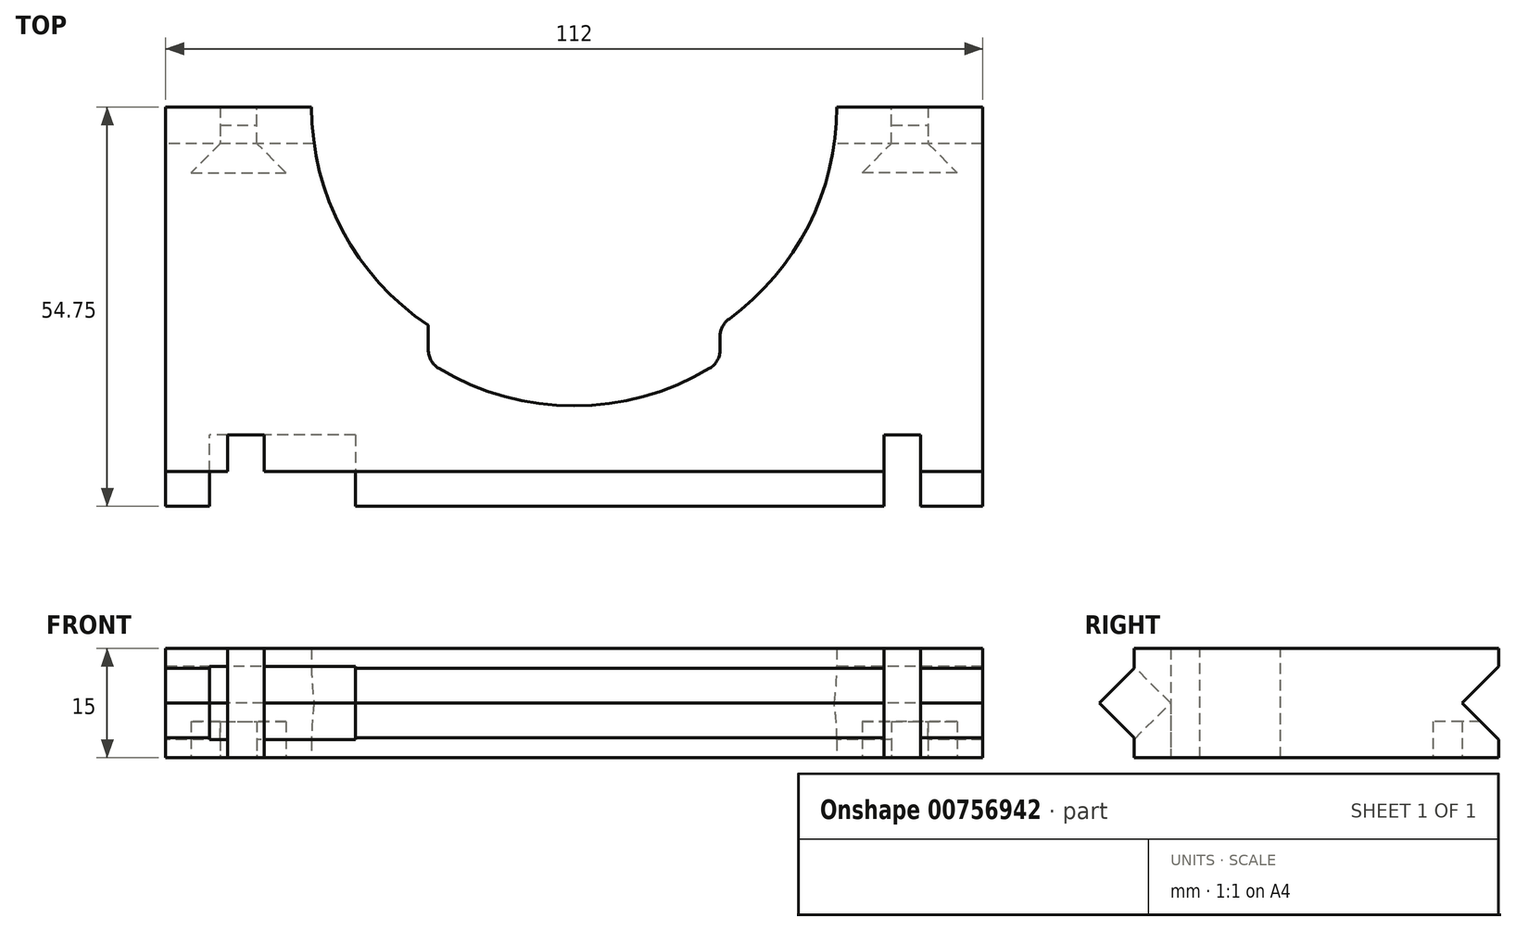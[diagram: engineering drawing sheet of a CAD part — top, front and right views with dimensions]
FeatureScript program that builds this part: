
annotation { "Feature Type Name" : "Feature", "Feature Type Description" : "" }
export const myFeature = defineFeature(function(context is Context, id is Id, definition is map)
    precondition{}
    {
        {
            var Q0;
            Q0=qCreatedBy(makeId("Top.planeOp"),FACE);
            var sketch = newSketch(context, id + "F0", { "sketchPlane" : qUnion([Q0])});
            skLineSegment(sketch, "E0", {"start": v(-56, 0) * mm, "end": v(56, 0) * mm});
            skLineSegment(sketch, "E1", {"start": v(56, 0) * mm, "end": v(56, 50) * mm});
            skLineSegment(sketch, "E2", {"start": v(56, 50) * mm, "end": v(36, 50) * mm});
            skLineSegment(sketch, "E3", {"start": v(-56, 0) * mm, "end": v(-56, 50) * mm});
            skLineSegment(sketch, "E4", {"start": v(-56, 50) * mm, "end": v(-36, 50) * mm});
            skArc(sketch, "E5", {"start": v(-36, 50) * mm, "mid": v(0, 14) * mm, "end": v(36, 50) * mm});
            skSolve(sketch);
        }
        {
            var Q0;
            Q0 = qSketchRegion(id + "F0", true);
            extrude(context, id + "F1", {"entities" : qUnion([Q0]), "depth" : 15 * mm, "offsetDistance" : 25 * mm});
        }
        {
            var Q0;
            Q0=makeQuery(id+"F1.opExtrude","SWEPT_FACE",FACE,{"disambiguationData":[OSD([sQuery(id+"F0.wireOp",EDGE,"E3")])]});
            var sketch = newSketch(context, id + "F2", { "sketchPlane" : qUnion([Q0])});
            skLineSegment(sketch, "E6", {"start": v(-50, 2.5) * mm, "end": v(-45, 7.5) * mm});
            skPoint(sketch, "E6.endSnap0", {"position": v(-50, 7.5) * mm});
            skLineSegment(sketch, "E7", {"start": v(-45, 7.5) * mm, "end": v(-50, 12.5) * mm});
            skLineSegment(sketch, "E8", {"start": v(-50, 12.5) * mm, "end": v(-50, 2.5) * mm});
            skSolve(sketch);
        }
        {
            var Q0;
            Q0 = qSketchRegion(id + "F2", true);
            extrude(context, id + "F3", {"entities" : qUnion([Q0]), "operationType" : NewBodyOperationType.REMOVE, "endBound" : BoundingType.THROUGH_ALL, "oppositeDirection" : true, "depth" : 25 * mm, "offsetDistance" : 25 * mm});
        }
        {
            var Q0;
            Q0=makeQuery(id+"F1.opExtrude","CAP_FACE",FACE,{"disambiguationData":[OSD([sQuery(id+"F0.wireOp",EDGE,"E0"),sQuery(id+"F0.wireOp",EDGE,"E1"),sQuery(id+"F0.wireOp",EDGE,"E2"),sQuery(id+"F0.wireOp",EDGE,"E3"),sQuery(id+"F0.wireOp",EDGE,"E4"),sQuery(id+"F0.wireOp",EDGE,"E5")])],"isStart":true});
            var sketch = newSketch(context, id + "F4", { "sketchPlane" : qUnion([Q0])});
            skLineSegment(sketch, "E9", {"start": v(-48.5, -50) * mm, "end": v(-48.5, -45) * mm});
            skLineSegment(sketch, "E10", {"start": v(-48.5, -45) * mm, "end": v(-52.5, -41) * mm});
            skLineSegment(sketch, "E11", {"start": v(-52.5, -41) * mm, "end": v(-39.5, -41) * mm});
            skLineSegment(sketch, "E12", {"start": v(-39.5, -41) * mm, "end": v(-43.5, -45) * mm});
            skLineSegment(sketch, "E13", {"start": v(-43.5, -45) * mm, "end": v(-43.5, -50) * mm});
            skLineSegment(sketch, "E14", {"start": v(-43.5, -50) * mm, "end": v(-48.5, -50) * mm});
            skLineSegment(sketch, "E15.MirrorCS", {"start": v(52.5, -41) * mm, "end": v(39.5, -41) * mm});
            skLineSegment(sketch, "E16.MirrorCS", {"start": v(48.5, -45) * mm, "end": v(52.5, -41) * mm});
            skLineSegment(sketch, "E17.MirrorCS", {"start": v(39.5, -41) * mm, "end": v(43.5, -45) * mm});
            skLineSegment(sketch, "E18.MirrorCS", {"start": v(48.5, -50) * mm, "end": v(48.5, -45) * mm});
            skLineSegment(sketch, "E19.MirrorCS", {"start": v(43.5, -45) * mm, "end": v(43.5, -50) * mm});
            skLineSegment(sketch, "E20.MirrorCS", {"start": v(43.5, -50) * mm, "end": v(48.5, -50) * mm});
            skSolve(sketch);
        }
        {
            var Q0;
            Q0=makeQuery(id+"F4.imprint","IMPRINT",FACE,{"disambiguationData":[TD([[makeQuery(id+"F4.imprint","IMPRINT",EDGE,{"derivedFrom":sQuery(id+"F4.wireOp",EDGE,"E9")}),-1.0]])]});
            var Q1;
            Q1=makeQuery(id+"F4.imprint","IMPRINT",FACE,{"disambiguationData":[TD([[makeQuery(id+"F4.imprint","IMPRINT",EDGE,{"derivedFrom":sQuery(id+"F4.wireOp",EDGE,"E15.MirrorCS")}),1.0]])]});
            extrude(context, id + "F5", {"entities" : qUnion([Q0, Q1]), "operationType" : NewBodyOperationType.REMOVE, "oppositeDirection" : true, "depth" : 5 * mm, "offsetDistance" : 25 * mm});
        }
        {
            var Q0;
            Q0=makeQuery(id+"F1.opExtrude","SWEPT_FACE",FACE,{"disambiguationData":[OSD([sQuery(id+"F0.wireOp",EDGE,"E3")])]});
            var sketch = newSketch(context, id + "F6", { "sketchPlane" : qUnion([Q0])});
            skLineSegment(sketch, "E21", {"start": v(0, 12.25) * mm, "end": v(0, 2.75) * mm});
            skLineSegment(sketch, "E22", {"start": v(0, 2.75) * mm, "end": v(4.75, 7.5) * mm});
            skLineSegment(sketch, "E23", {"start": v(4.75, 7.5) * mm, "end": v(0, 12.25) * mm});
            skSolve(sketch);
        }
        {
            var Q0;
            Q0 = qSketchRegion(id + "F6", true);
            var Q1;
            Q1=makeQuery(id+"F1.opExtrude","SWEPT_FACE",FACE,{"disambiguationData":[OSD([sQuery(id+"F0.wireOp",EDGE,"E1")])]});
            extrude(context, id + "F7", {"entities" : qUnion([Q0]), "operationType" : NewBodyOperationType.ADD, "endBound" : BoundingType.UP_TO_SURFACE, "oppositeDirection" : true, "depth" : 25 * mm, "endBoundEntityFace" : qUnion([Q1]), "offsetDistance" : 25 * mm});
        }
        {
            var Q0;
            Q0=makeQuery(id+"F1.opExtrude","CAP_FACE",FACE,{"disambiguationData":[OSD([sQuery(id+"F0.wireOp",EDGE,"E0"),sQuery(id+"F0.wireOp",EDGE,"E1"),sQuery(id+"F0.wireOp",EDGE,"E2"),sQuery(id+"F0.wireOp",EDGE,"E3"),sQuery(id+"F0.wireOp",EDGE,"E4"),sQuery(id+"F0.wireOp",EDGE,"E5")])],"isStart":true});
            var sketch = newSketch(context, id + "F8", { "sketchPlane" : qUnion([Q0])});
            skLineSegment(sketch, "E24", {"start": v(-47.5, 0) * mm, "end": v(-47.5, -5) * mm});
            skLineSegment(sketch, "E25", {"start": v(-47.5, -5) * mm, "end": v(-42.5, -5) * mm});
            skLineSegment(sketch, "E26", {"start": v(-42.5, -5) * mm, "end": v(-42.5, 0) * mm});
            skLineSegment(sketch, "E27", {"start": v(-42.5, 0) * mm, "end": v(-47.5, 0) * mm, "construction": true});
            skLineSegment(sketch, "E28", {"start": v(-47.5, 0) * mm, "end": v(-47.5, 11.28) * mm});
            skLineSegment(sketch, "E29", {"start": v(-47.5, 11.28) * mm, "end": v(-42.5, 11.28) * mm});
            skLineSegment(sketch, "E30", {"start": v(-42.5, 11.28) * mm, "end": v(-42.5, 0) * mm});
            skLineSegment(sketch, "E31.MirrorCS", {"start": v(42.5, 11.28) * mm, "end": v(42.5, 0) * mm});
            skLineSegment(sketch, "E32.MirrorCS", {"start": v(42.5, -5) * mm, "end": v(42.5, 0) * mm});
            skLineSegment(sketch, "E33.MirrorCS", {"start": v(47.5, 0) * mm, "end": v(47.5, 11.28) * mm});
            skLineSegment(sketch, "E34.MirrorCS", {"start": v(42.5, 0) * mm, "end": v(47.5, 0) * mm, "construction": true});
            skLineSegment(sketch, "E35.MirrorCS", {"start": v(47.5, 11.28) * mm, "end": v(42.5, 11.28) * mm});
            skLineSegment(sketch, "E36.MirrorCS", {"start": v(47.5, -5) * mm, "end": v(42.5, -5) * mm});
            skLineSegment(sketch, "E37.MirrorCS", {"start": v(47.5, 0) * mm, "end": v(47.5, -5) * mm});
            skSolve(sketch);
        }
        {
            var Q0;
            Q0 = qSketchRegion(id + "F8", true);
            extrude(context, id + "F9", {"entities" : qUnion([Q0]), "operationType" : NewBodyOperationType.REMOVE, "oppositeDirection" : true, "depth" : 25 * mm, "offsetDistance" : 25 * mm});
        }
        {
            var Q0;
            Q0=makeQuery(id+"F9.boolean.opBoolean","COPY",FACE,{"derivedFrom":makeQuery(id+"F9.opExtrude","SWEPT_FACE",FACE,{"disambiguationData":[OSD([sQuery(id+"F8.wireOp",EDGE,"E26"),sQuery(id+"F8.wireOp",EDGE,"E30")])]})});
            var Q1;
            Q1=makeQuery(id+"F9.boolean.opBoolean","COPY",FACE,{"derivedFrom":makeQuery(id+"F9.opExtrude","SWEPT_FACE",FACE,{"disambiguationData":[OSD([sQuery(id+"F8.wireOp",EDGE,"E24"),sQuery(id+"F8.wireOp",EDGE,"E28")])]})});
            cPlane(context, id + "F10", {"entities" : qUnion([Q0, Q1]), "cplaneType" : CPlaneType.MID_PLANE, "offset" : 25 * mm, "width" : 150 * mm, "height" : 150 * mm});
        }
        {
            var Q0;
            Q0=qCreatedBy(id+"F10.planeOp",FACE);
            var sketch = newSketch(context, id + "F11", { "sketchPlane" : qUnion([Q0])});
            skLineSegment(sketch, "E38.0", {"start": v(0, 15) * mm, "end": v(0, 12.25) * mm, "construction": true});
            skLineSegment(sketch, "E39.0", {"start": v(0, 2.75) * mm, "end": v(0, 0) * mm, "construction": true});
            skLineSegment(sketch, "E40", {"start": v(-5, 7.5) * mm, "end": v(0, 12.5) * mm});
            skLineSegment(sketch, "E41", {"start": v(0, 2.5) * mm, "end": v(-5, 7.5) * mm});
            skLineSegment(sketch, "E42", {"start": v(0, 12.5) * mm, "end": v(5, 7.5) * mm});
            skLineSegment(sketch, "E43", {"start": v(5, 7.5) * mm, "end": v(0, 2.5) * mm});
            skSolve(sketch);
        }
        {
            var Q0;
            Q0=makeQuery(id+"F11.imprint","IMPRINT",FACE,{"disambiguationData":[TD([[makeQuery(id+"F11.imprint","IMPRINT",EDGE,{"derivedFrom":sQuery(id+"F11.wireOp",EDGE,"E40")}),-1.0]])]});
            extrude(context, id + "F12", {"entities" : qUnion([Q0]), "operationType" : NewBodyOperationType.REMOVE, "oppositeDirection" : true, "depth" : 15 * mm, "offsetDistance" : 25 * mm, "hasSecondDirection" : true, "secondDirectionOppositeDirection" : false, "secondDirectionDepth" : 5 * mm});
        }
        {
            var Q0;
            Q0=makeQuery(id+"F1.opExtrude","CAP_FACE",FACE,{"disambiguationData":[OSD([sQuery(id+"F0.wireOp",EDGE,"E0"),sQuery(id+"F0.wireOp",EDGE,"E1"),sQuery(id+"F0.wireOp",EDGE,"E2"),sQuery(id+"F0.wireOp",EDGE,"E3"),sQuery(id+"F0.wireOp",EDGE,"E4"),sQuery(id+"F0.wireOp",EDGE,"E5")])],"isStart":false});
            var sketch = newSketch(context, id + "F13", { "sketchPlane" : qUnion([Q0])});
            skLineSegment(sketch, "E44", {"start": v(20, 20.07) * mm, "end": v(20, 15.07) * mm});
            skLineSegment(sketch, "E45", {"start": v(20, 15.07) * mm, "end": v(-20, 15.07) * mm, "construction": true});
            skLineSegment(sketch, "E46", {"start": v(-20, 15.07) * mm, "end": v(-20, 20.07) * mm});
            skArc(sketch, "E47", {"start": v(-20, 20.07) * mm, "mid": v(0, 14) * mm, "end": v(20, 20.07) * mm});
            skArc(sketch, "E48", {"start": v(-20, 15.07) * mm, "mid": v(0, 9) * mm, "end": v(20, 15.07) * mm});
            skSolve(sketch);
        }
        {
            var Q0;
            Q0=makeQuery(id+"F13.imprint","IMPRINT",FACE,{"disambiguationData":[TD([[makeQuery(id+"F13.imprint","IMPRINT",EDGE,{"derivedFrom":sQuery(id+"F13.wireOp",EDGE,"E44")}),-1.0]])]});
            extrude(context, id + "F14", {"entities" : qUnion([Q0]), "operationType" : NewBodyOperationType.REMOVE, "oppositeDirection" : true, "depth" : 25 * mm, "offsetDistance" : 25 * mm});
        }
        {
            var Q0;
            Q0=makeQuery(id+"F14.boolean.opBoolean","COPY",EDGE,{"derivedFrom":makeQuery(id+"F14.opExtrude","SWEPT_EDGE",EDGE,{"disambiguationData":[OSD([sQuery(id+"F0.wireOp",EDGE,"E5"),sQuery(id+"F13.wireOp",EDGE,"E46"),sQuery(id+"F13.wireOp",EDGE,"E47")])]})});
            var Q1;
            Q1=makeQuery(id+"F14.boolean.opBoolean","COPY",EDGE,{"derivedFrom":makeQuery(id+"F14.opExtrude","SWEPT_EDGE",EDGE,{"disambiguationData":[OSD([sQuery(id+"F0.wireOp",EDGE,"E5"),sQuery(id+"F13.wireOp",EDGE,"E44"),sQuery(id+"F13.wireOp",EDGE,"E47")])]})});
            var Q2;
            Q2=makeQuery(id+"F14.boolean.opBoolean","COPY",EDGE,{"derivedFrom":makeQuery(id+"F14.opExtrude","SWEPT_EDGE",EDGE,{"disambiguationData":[OSD([sQuery(id+"F13.wireOp",EDGE,"E46"),sQuery(id+"F13.wireOp",EDGE,"E48")])]})});
            var Q3;
            Q3=makeQuery(id+"F14.boolean.opBoolean","COPY",EDGE,{"derivedFrom":makeQuery(id+"F14.opExtrude","SWEPT_EDGE",EDGE,{"disambiguationData":[OSD([sQuery(id+"F13.wireOp",EDGE,"E44"),sQuery(id+"F13.wireOp",EDGE,"E48")])]})});
            fillet(context, id + "F15", {"entities" : qUnion([Q0, Q1, Q2, Q3]), "radius" : 3 * mm, "tangentPropagation" : true, "allowEdgeOverflow" : false});
        }
    });
